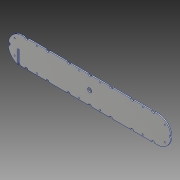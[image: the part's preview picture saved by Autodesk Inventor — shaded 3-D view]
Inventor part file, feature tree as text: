
AUTODESK INVENTOR PART (.ipt)
format: ipt  version: 2020 (Build 240168000, 168)  size: 334,848 bytes
history: native  units: mm
features: extrude x5, sketch x4
ambient origin geometry x8: Origin, YZ Plane, XZ Plane, XY Plane, X Axis, Y Axis, Z Axis, Center Point
bodies: Solid1 (feature_tree)
feature tree (9):
  extrude  "Extrusion1"  Depth=432.0mm
  extrude  "Extrusion3"  Depth=6.2mm TaperAngle=0.0deg
  extrude  "Extrusion7"  Depth=10.0mm
  extrude  "Extrusion10"  Depth=10.0mm
  extrude  "Extrusion11"  Depth=10.0mm
  sketch  "Sketch4"  dims[d4=432.0mm d5=864.0mm]
  sketch  "Sketch10"  dims[d7=86.0mm d9=6.2mm d10=0.0mm]
  sketch  "Sketch13"  dims[d18=20.0mm d21=10.0mm]
  sketch  "Sketch14"  dims[d22=150.0mm d23=150.0mm d24=150.0mm d25=150.0mm d26=150.0mm d27=150.0mm d28=10.0mm d29=10.0mm d30=10.0mm d31=0.0mm d54=76.0mm d55=48.0mm d59=48.0mm d60=76.0mm d73=8.0mm d107=172.0mm d109=135.0mm d110=135.0mm d111=135.0mm d112=135.0mm d113=135.0mm d115=135.0mm d116=20.0mm d120=48.0mm d121=38.0mm d122=38.0mm d123=48.0mm d124=38.0mm d125=38.0mm d130=76.0mm d131=76.0mm d144=76.0mm d145=76.0mm d146=76.0mm d147=76.0mm d149=57.5mm d150=57.5mm d151=57.5mm d152=57.5mm d153=57.5mm d154=57.5mm d155=57.5mm d156=57.5mm d157=0.0mm d158=0.0mm d163=9.0mm d164=460.0mm d165=7.0mm d166=30.0mm d167=30.0mm d168=460.0mm d169=15.0mm d173=20.0mm d174=0.0mm d175=0.0mm d182=6.981317mm d183=12.217305mm d185=10.0mm d186=0.0mm]
